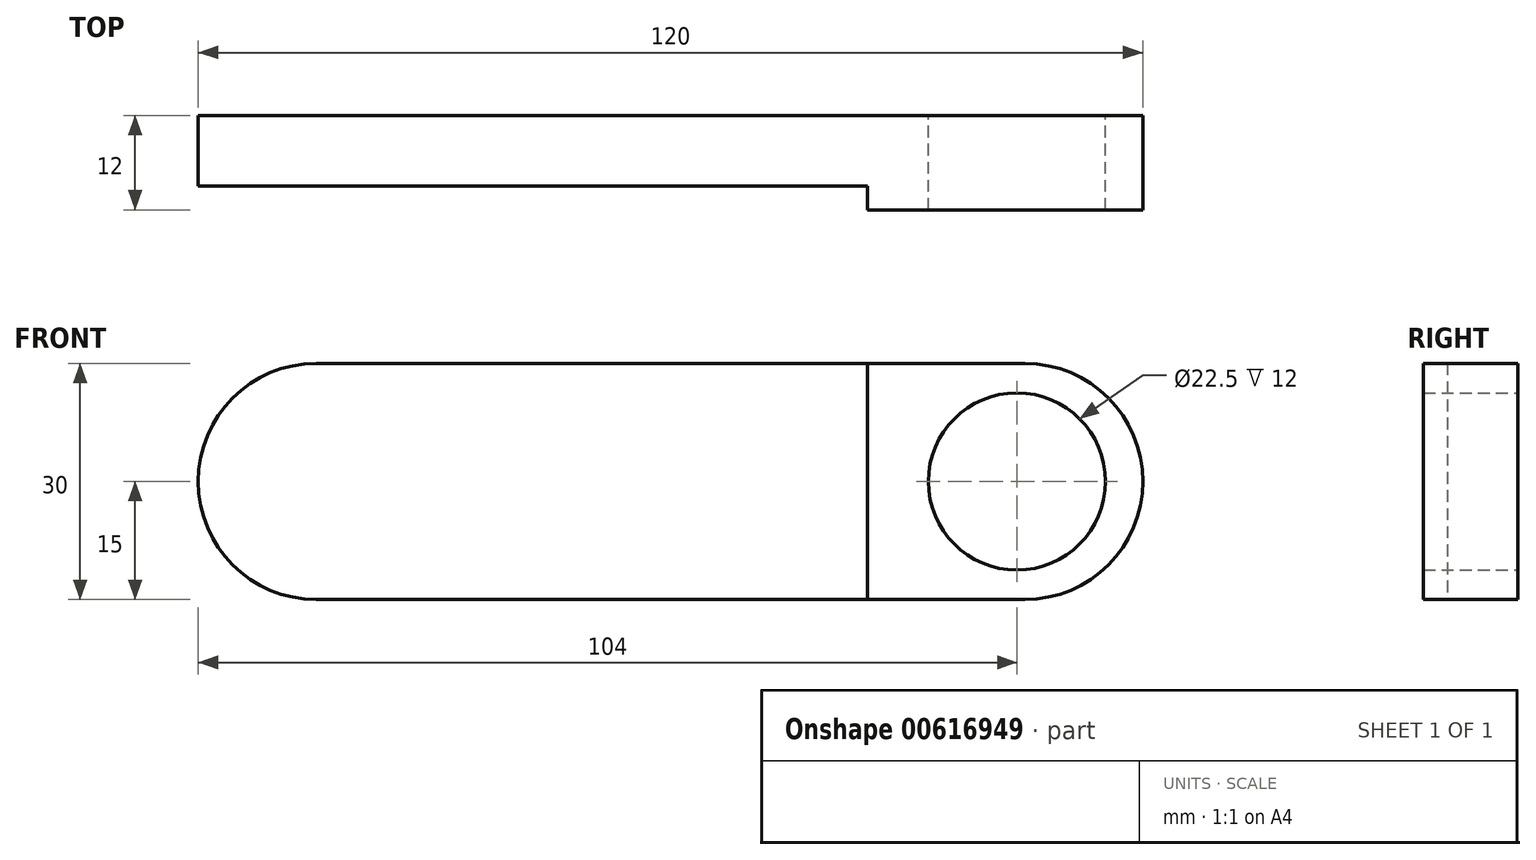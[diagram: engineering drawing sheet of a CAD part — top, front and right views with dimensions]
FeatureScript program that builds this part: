
annotation { "Feature Type Name" : "Feature", "Feature Type Description" : "" }
export const myFeature = defineFeature(function(context is Context, id is Id, definition is map)
    precondition{}
    {
        {
            var Q0;
            Q0=qCreatedBy(makeId("Front.planeOp"),FACE);
            var sketch = newSketch(context, id + "F0", { "sketchPlane" : qUnion([Q0])});
            skLineSegment(sketch, "E0.bottom", {"start": v(45, -15) * mm, "end": v(-45, -15) * mm});
            skLineSegment(sketch, "E0.top", {"start": v(45, 15) * mm, "end": v(-45, 15) * mm});
            skLineSegment(sketch, "E0.left", {"start": v(60, 0) * mm, "end": v(60, 0) * mm});
            skLineSegment(sketch, "E0.right", {"start": v(-60, 0) * mm, "end": v(-60, 0) * mm});
            skPoint(sketch, "E0.middle", {"position": v(0, 0) * mm});
            skPoint(sketch, "E1", {"position": v(44, 0) * mm});
            skCircle(sketch, "E2", {"center": v(44, 0) * mm, "radius": 11.25 * mm});
            skPoint(sketch, "E3.visualSharp", {"position": v(-60, 15) * mm});
            skArc(sketch, "E3.filletArc", {"start": v(-45, 15) * mm, "mid": v(-55.6, 10.6) * mm, "end": v(-60, 0) * mm});
            skPoint(sketch, "E4.visualSharp", {"position": v(-60, -15) * mm});
            skArc(sketch, "E4.filletArc", {"start": v(-60, 0) * mm, "mid": v(-55.6, -10.6) * mm, "end": v(-45, -15) * mm});
            skPoint(sketch, "E5.visualSharp", {"position": v(60, -15) * mm});
            skArc(sketch, "E5.filletArc", {"start": v(45, -15) * mm, "mid": v(55.6, -10.6) * mm, "end": v(60, 0) * mm});
            skPoint(sketch, "E6.visualSharp", {"position": v(60, 15) * mm});
            skArc(sketch, "E6.filletArc", {"start": v(60, 0) * mm, "mid": v(55.6, 10.6) * mm, "end": v(45, 15) * mm});
            skLineSegment(sketch, "E7", {"start": v(25, 15) * mm, "end": v(25, -15) * mm});
            skPoint(sketch, "E8.orphan", {"position": v(44, 15) * mm});
            skPoint(sketch, "E9.orphan", {"position": v(44, -15) * mm});
            skSolve(sketch);
        }
        {
            var Q0;
            Q0=makeQuery(id+"F0.imprint","IMPRINT",FACE,{"disambiguationData":[TD([[makeQuery(id+"F0.imprint","IMPRINT",EDGE,{"derivedFrom":sQuery(id+"F0.wireOp",EDGE,"E2")}),-1.0]])]});
            extrude(context, id + "F1", {"entities" : qUnion([Q0]), "depth" : 12 * mm, "offsetDistance" : 25 * mm});
        }
        {
            var Q0;
            {var subQ0=sQuery(id+"F0.wireOp",EDGE,"E3.filletArc");Q0=makeQuery(id+"F0.imprint","IMPRINT",FACE,{"disambiguationData":[TD([[makeQuery(id+"F0.imprint","IMPRINT",EDGE,{"derivedFrom":subQ0}),1.0]])]});}
            extrude(context, id + "F2", {"entities" : qUnion([Q0]), "operationType" : NewBodyOperationType.ADD, "depth" : 9 * mm, "offsetDistance" : 25 * mm});
        }
    });
